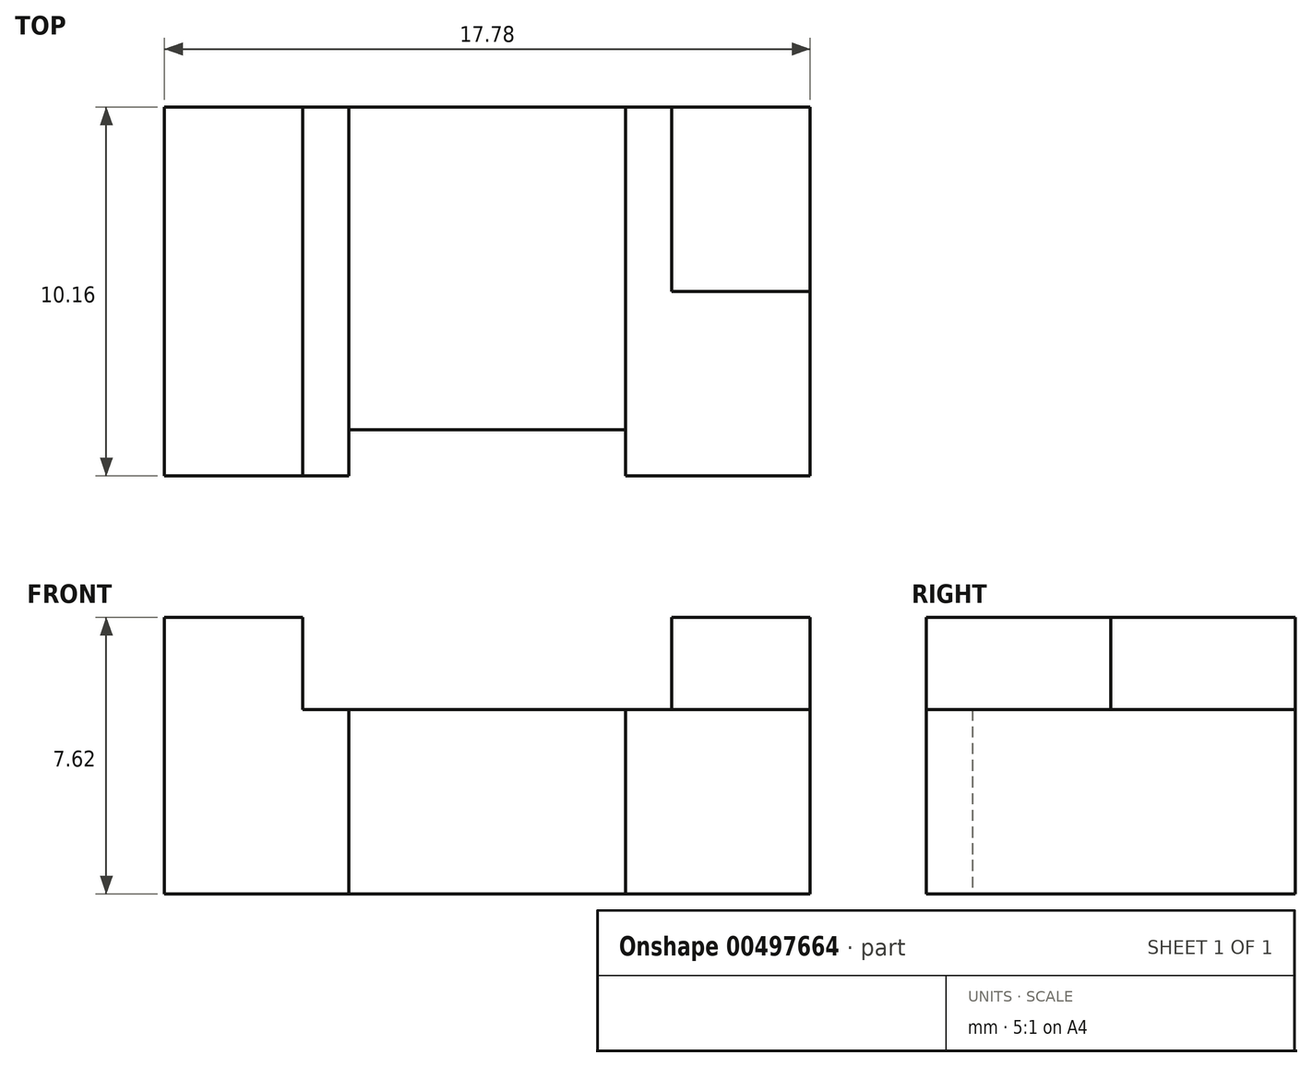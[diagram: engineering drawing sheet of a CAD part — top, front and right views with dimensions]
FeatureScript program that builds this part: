
annotation { "Feature Type Name" : "Feature", "Feature Type Description" : "" }
export const myFeature = defineFeature(function(context is Context, id is Id, definition is map)
    precondition{}
    {
        {
            var Q0;
            Q0=qCreatedBy(makeId("Front.planeOp"),FACE);
            var sketch = newSketch(context, id + "F0", { "sketchPlane" : qUnion([Q0])});
            skLineSegment(sketch, "E0", {"start": v(-18.9, 19.39) * mm, "end": v(-18.9, -35.48) * mm, "construction": true});
            skLineSegment(sketch, "E1", {"start": v(-10, 13.17) * mm, "end": v(-10, 0.47) * mm});
            skLineSegment(sketch, "E2", {"start": v(-10, 0.47) * mm, "end": v(-13.82, -12.23) * mm});
            skLineSegment(sketch, "E3", {"start": v(-13.82, -12.23) * mm, "end": v(-15.72, -12.23) * mm});
            skLineSegment(sketch, "E4", {"start": v(-15.72, -12.23) * mm, "end": v(-15.72, -4.61) * mm});
            skLineSegment(sketch, "E5", {"start": v(-15.72, -4.61) * mm, "end": v(-18.9, -4.61) * mm});
            skLineSegment(sketch, "E6", {"start": v(-10, 13.17) * mm, "end": v(-10, 10.63) * mm});
            skLineSegment(sketch, "E7", {"start": v(-10, 10.63) * mm, "end": v(-13.82, 10.63) * mm});
            skLineSegment(sketch, "E8", {"start": v(-13.82, 10.63) * mm, "end": v(-13.82, 13.17) * mm});
            skLineSegment(sketch, "E9", {"start": v(-10, 10.63) * mm, "end": v(-10, 5.55) * mm});
            skLineSegment(sketch, "E10", {"start": v(-10, 5.55) * mm, "end": v(-15.09, 5.55) * mm});
            skLineSegment(sketch, "E11", {"start": v(-13.82, 10.63) * mm, "end": v(-15.09, 10.63) * mm});
            skLineSegment(sketch, "E12", {"start": v(-15.09, 10.63) * mm, "end": v(-15.09, 5.55) * mm});
            skLineSegment(sketch, "E13", {"start": v(-15.09, 5.55) * mm, "end": v(-18.9, 5.55) * mm});
            skLineSegment(sketch, "E14", {"start": v(-15.09, 10.63) * mm, "end": v(-18.9, 10.63) * mm});
            skPoint(sketch, "E15", {"position": v(-13.82, 13.17) * mm});
            skLineSegment(sketch, "E16", {"start": v(-13.82, 13.17) * mm, "end": v(-10, 13.17) * mm});
            skLineSegment(sketch, "E17.MirrorCS", {"start": v(-22.7, 10.63) * mm, "end": v(-18.9, 10.63) * mm});
            skLineSegment(sketch, "E18.MirrorCS", {"start": v(-22.7, 5.55) * mm, "end": v(-18.9, 5.55) * mm});
            skLineSegment(sketch, "E19.MirrorCS", {"start": v(-22.7, 10.63) * mm, "end": v(-22.7, 5.55) * mm});
            skLineSegment(sketch, "E20.MirrorCS", {"start": v(-27.79, 5.55) * mm, "end": v(-22.7, 5.55) * mm});
            skLineSegment(sketch, "E21.MirrorCS", {"start": v(-27.79, 10.63) * mm, "end": v(-23.98, 10.63) * mm});
            skLineSegment(sketch, "E22.MirrorCS", {"start": v(-23.98, 10.63) * mm, "end": v(-22.7, 10.63) * mm});
            skLineSegment(sketch, "E23.MirrorCS", {"start": v(-23.98, 10.63) * mm, "end": v(-23.98, 13.17) * mm});
            skLineSegment(sketch, "E24.MirrorCS", {"start": v(-23.98, 13.17) * mm, "end": v(-27.79, 13.17) * mm});
            skLineSegment(sketch, "E25.MirrorCS", {"start": v(-27.79, 13.17) * mm, "end": v(-27.79, 10.63) * mm});
            skLineSegment(sketch, "E26.MirrorCS", {"start": v(-27.79, 10.63) * mm, "end": v(-27.79, 5.55) * mm});
            skLineSegment(sketch, "E27.MirrorCS", {"start": v(-27.79, 13.17) * mm, "end": v(-27.79, 0.47) * mm});
            skLineSegment(sketch, "E28.MirrorCS", {"start": v(-27.79, 0.47) * mm, "end": v(-23.98, -12.23) * mm});
            skLineSegment(sketch, "E29.MirrorCS", {"start": v(-23.98, -12.23) * mm, "end": v(-22.07, -12.23) * mm});
            skLineSegment(sketch, "E30.MirrorCS", {"start": v(-22.07, -12.23) * mm, "end": v(-22.07, -4.61) * mm});
            skLineSegment(sketch, "E31.MirrorCS", {"start": v(-22.07, -4.61) * mm, "end": v(-18.9, -4.61) * mm});
            skSolve(sketch);
        }
        {
            var Q0;
            {var subQ0=sQuery(id+"F0.wireOp",EDGE,"E21.MirrorCS");Q0=makeQuery(id+"F0.imprint","IMPRINT",FACE,{"disambiguationData":[TD([[makeQuery(id+"F0.imprint","IMPRINT",EDGE,{"derivedFrom":subQ0}),1.0]])]});}
            var Q1;
            Q1=makeQuery(id+"F0.imprint","IMPRINT",FACE,{"disambiguationData":[TD([[makeQuery(id+"F0.imprint","IMPRINT",EDGE,{"derivedFrom":sQuery(id+"F0.wireOp",EDGE,"E6")}),-1.0]])]});
            var Q2;
            Q2=makeQuery(id+"F0.imprint","IMPRINT",FACE,{"disambiguationData":[TD([[makeQuery(id+"F0.imprint","IMPRINT",EDGE,{"derivedFrom":sQuery(id+"F0.wireOp",EDGE,"E19.MirrorCS")}),-1.0]])]});
            var Q3;
            Q3=makeQuery(id+"F0.imprint","IMPRINT",FACE,{"disambiguationData":[TD([[makeQuery(id+"F0.imprint","IMPRINT",EDGE,{"derivedFrom":sQuery(id+"F0.wireOp",EDGE,"E7")}),1.0]])]});
            extrude(context, id + "F1", {"entities" : qUnion([Q0, Q1, Q2, Q3]), "depth" : 10.16 * mm});
        }
        {
            var Q0;
            Q0=makeQuery(id+"F0.imprint","IMPRINT",FACE,{"disambiguationData":[TD([[makeQuery(id+"F0.imprint","IMPRINT",EDGE,{"derivedFrom":sQuery(id+"F0.wireOp",EDGE,"E12")}),-1.0]])]});
            extrude(context, id + "F2", {"entities" : qUnion([Q0]), "depth" : 8.9 * mm});
        }
        {
            var Q0;
            Q0=makeQuery(id+"F0.imprint","IMPRINT",FACE,{"disambiguationData":[TD([[makeQuery(id+"F0.imprint","IMPRINT",EDGE,{"derivedFrom":sQuery(id+"F0.wireOp",EDGE,"E1")}),-1.0]])]});
            extrude(context, id + "F3", {"entities" : qUnion([Q0]), "depth" : 5.08 * mm});
        }
    });
